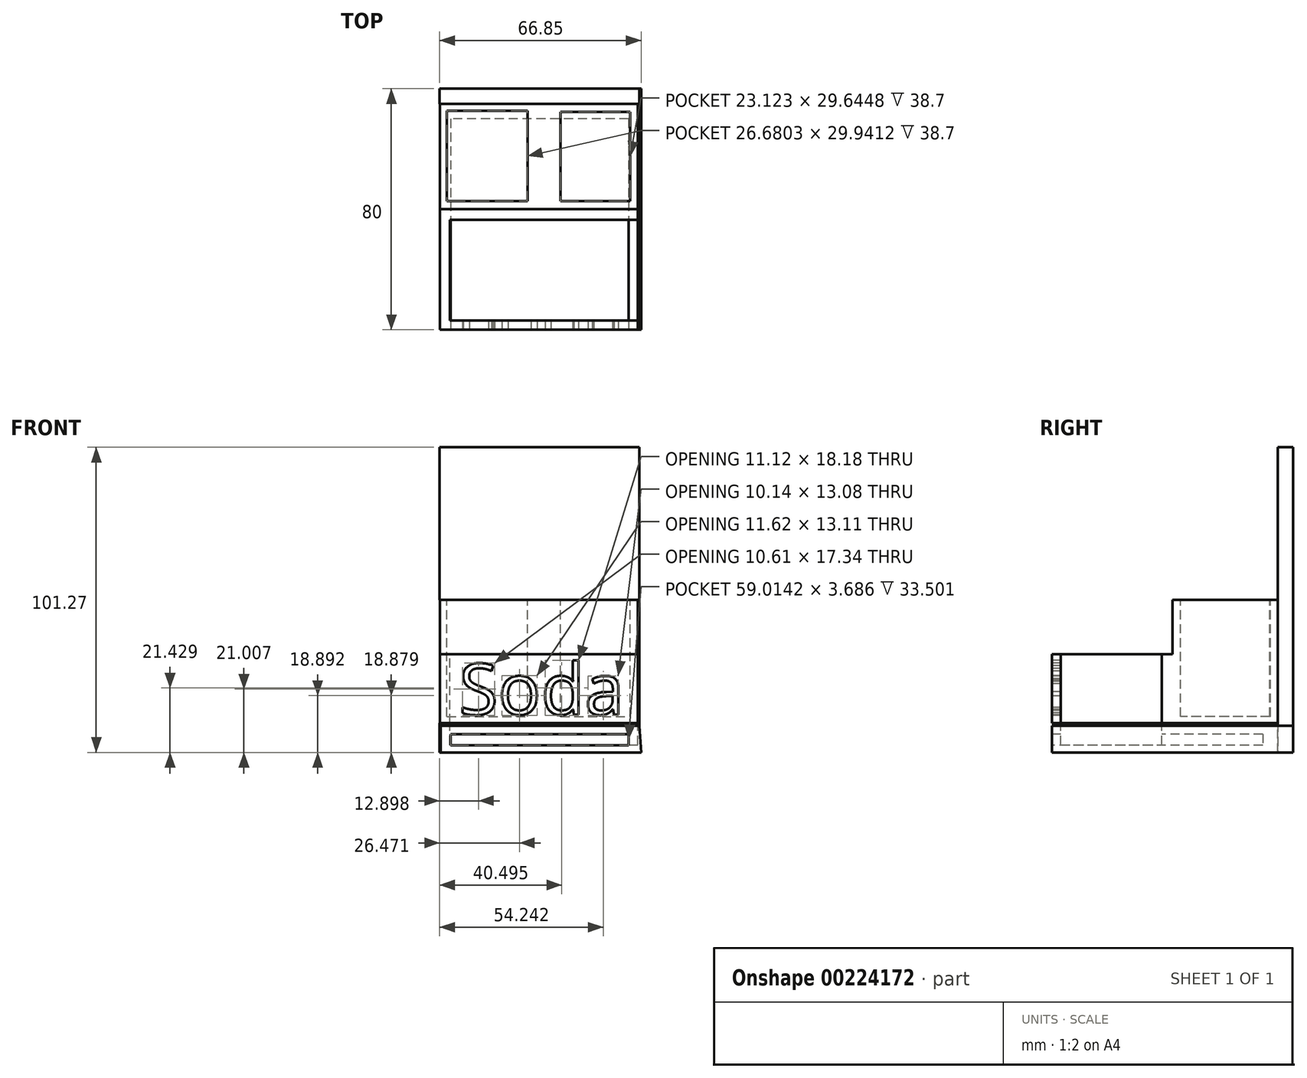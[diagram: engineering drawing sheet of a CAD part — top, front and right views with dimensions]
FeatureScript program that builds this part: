
annotation { "Feature Type Name" : "Feature", "Feature Type Description" : "" }
export const myFeature = defineFeature(function(context is Context, id is Id, definition is map)
    precondition{}
    {
        {
            var Q0;
            Q0=qCreatedBy(makeId("Front.planeOp"),FACE);
            var sketch = newSketch(context, id + "F0", { "sketchPlane" : qUnion([Q0])});
            skLineSegment(sketch, "E0.bottom", {"start": v(-34.43, 50.63) * mm, "end": v(31.85, 50.63) * mm});
            skLineSegment(sketch, "E0.top", {"start": v(-34.43, -50.63) * mm, "end": v(31.85, -50.63) * mm});
            skLineSegment(sketch, "E0.left", {"start": v(-34.43, 50.63) * mm, "end": v(-34.43, -50.63) * mm});
            skLineSegment(sketch, "E0.right", {"start": v(31.85, 50.63) * mm, "end": v(31.85, -50.63) * mm});
            skSolve(sketch);
        }
        {
            var Q0;
            Q0=makeQuery(id+"F0.imprint","IMPRINT",FACE,{"disambiguationData":[TD([[makeQuery(id+"F0.imprint","IMPRINT",EDGE,{"derivedFrom":sQuery(id+"F0.wireOp",EDGE,"E0.bottom")}),-1.0]])]});
            extrude(context, id + "F1", {"entities" : qUnion([Q0]), "depth" : 5 * mm});
        }
        {
            var Q0;
            Q0=qCreatedBy(makeId("Front.planeOp"),FACE);
            var sketch = newSketch(context, id + "F2", { "sketchPlane" : qUnion([Q0])});
            skLineSegment(sketch, "E1", {"start": v(-34.14, -41.74) * mm, "end": v(31.84, -41.74) * mm});
            skLineSegment(sketch, "E2", {"start": v(-34.14, -41.74) * mm, "end": v(-34.14, -50.64) * mm});
            skLineSegment(sketch, "E3", {"start": v(-34.14, -50.64) * mm, "end": v(32.42, -50.64) * mm});
            skLineSegment(sketch, "E4", {"start": v(32.42, -50.64) * mm, "end": v(31.84, -41.74) * mm});
            skSolve(sketch);
        }
        {
            var Q0;
            Q0 = qSketchRegion(id + "F2", true);
            extrude(context, id + "F3", {"entities" : qUnion([Q0]), "operationType" : NewBodyOperationType.ADD, "depth" : 80 * mm});
        }
        {
            var Q0;
            Q0=makeQuery(id+"F3.opExtrude","CAP_FACE",FACE,{"disambiguationData":[OSD([sQuery(id+"F2.wireOp",EDGE,"E1"),sQuery(id+"F2.wireOp",EDGE,"E2"),sQuery(id+"F2.wireOp",EDGE,"E3"),sQuery(id+"F2.wireOp",EDGE,"E4")])],"isStart":false});
            var sketch = newSketch(context, id + "F4", { "sketchPlane" : qUnion([Q0])});
            skLineSegment(sketch, "E5.bottom", {"start": v(28.24, -44.55) * mm, "end": v(-30.78, -44.55) * mm});
            skLineSegment(sketch, "E5.top", {"start": v(28.24, -48.23) * mm, "end": v(-30.78, -48.23) * mm});
            skLineSegment(sketch, "E5.left", {"start": v(28.24, -44.55) * mm, "end": v(28.24, -48.23) * mm});
            skLineSegment(sketch, "E5.right", {"start": v(-30.78, -44.55) * mm, "end": v(-30.78, -48.23) * mm});
            skSolve(sketch);
        }
        {
            var Q0;
            Q0=makeQuery(id+"F4.imprint","IMPRINT",FACE,{"disambiguationData":[TD([[makeQuery(id+"F4.imprint","IMPRINT",EDGE,{"derivedFrom":sQuery(id+"F4.wireOp",EDGE,"E5.bottom")}),1.0]])]});
            extrude(context, id + "F5", {"entities" : qUnion([Q0]), "operationType" : NewBodyOperationType.REMOVE, "oppositeDirection" : true, "depth" : 70 * mm});
        }
        {
            var Q0;
            Q0=qCreatedBy(makeId("Front.planeOp"),FACE);
            var sketch = newSketch(context, id + "F6", { "sketchPlane" : qUnion([Q0])});
            skLineSegment(sketch, "E6.bottom", {"start": v(-34.43, 0) * mm, "end": v(0, 0) * mm});
            skLineSegment(sketch, "E6.top", {"start": v(-34.43, -40.88) * mm, "end": v(0, -40.88) * mm});
            skLineSegment(sketch, "E6.left", {"start": v(-34.43, 0) * mm, "end": v(-34.43, -40.88) * mm});
            skLineSegment(sketch, "E6.right", {"start": v(0, 0) * mm, "end": v(0, -40.88) * mm});
            skLineSegment(sketch, "E7.bottom", {"start": v(0, 0) * mm, "end": v(31.27, 0) * mm});
            skLineSegment(sketch, "E7.top", {"start": v(0, -40.88) * mm, "end": v(31.27, -40.88) * mm});
            skLineSegment(sketch, "E7.right", {"start": v(31.27, 0) * mm, "end": v(31.27, -40.88) * mm});
            skSolve(sketch);
        }
        {
            var Q0;
            Q0 = qSketchRegion(id + "F6", true);
            extrude(context, id + "F7", {"entities" : qUnion([Q0]), "operationType" : NewBodyOperationType.ADD, "depth" : 40 * mm});
        }
        {
            var Q0;
            Q0=qCreatedBy(makeId("Top.planeOp"),FACE);
            var sketch = newSketch(context, id + "F8", { "sketchPlane" : qUnion([Q0])});
            skLineSegment(sketch, "E8.bottom", {"start": v(-32.02, -7.4) * mm, "end": v(-5.34, -7.4) * mm});
            skLineSegment(sketch, "E8.top", {"start": v(-32.02, -37.33) * mm, "end": v(-5.34, -37.33) * mm});
            skLineSegment(sketch, "E8.left", {"start": v(-32.02, -7.4) * mm, "end": v(-32.02, -37.33) * mm});
            skLineSegment(sketch, "E8.right", {"start": v(-5.34, -7.4) * mm, "end": v(-5.34, -37.33) * mm});
            skLineSegment(sketch, "E9.bottom", {"start": v(5.63, -7.69) * mm, "end": v(28.76, -7.69) * mm});
            skLineSegment(sketch, "E9.top", {"start": v(5.63, -37.33) * mm, "end": v(28.76, -37.33) * mm});
            skLineSegment(sketch, "E9.left", {"start": v(5.63, -7.69) * mm, "end": v(5.63, -37.33) * mm});
            skLineSegment(sketch, "E9.right", {"start": v(28.76, -7.69) * mm, "end": v(28.76, -37.33) * mm});
            skSolve(sketch);
        }
        {
            var Q0;
            Q0 = qSketchRegion(id + "F8", true);
            extrude(context, id + "F9", {"entities" : qUnion([Q0]), "operationType" : NewBodyOperationType.REMOVE, "oppositeDirection" : true, "depth" : 38.7 * mm});
        }
        {
            var Q0;
            Q0=makeQuery(id+"F7.opExtrude","CAP_FACE",FACE,{"disambiguationData":[OSD([sQuery(id+"F6.wireOp",EDGE,"E6.bottom"),sQuery(id+"F6.wireOp",EDGE,"E6.top"),sQuery(id+"F6.wireOp",EDGE,"E6.left"),sQuery(id+"F6.wireOp",EDGE,"E7.bottom"),sQuery(id+"F6.wireOp",EDGE,"E7.top"),sQuery(id+"F6.wireOp",EDGE,"E7.right")])],"isStart":false});
            var sketch = newSketch(context, id + "F10", { "sketchPlane" : qUnion([Q0])});
            skLineSegment(sketch, "E10.bottom", {"start": v(-34.43, -18.1) * mm, "end": v(31.27, -18.1) * mm});
            skLineSegment(sketch, "E10.top", {"start": v(-34.43, -40.88) * mm, "end": v(31.27, -40.88) * mm});
            skLineSegment(sketch, "E10.left", {"start": v(-34.43, -18.1) * mm, "end": v(-34.43, -40.88) * mm});
            skLineSegment(sketch, "E10.right", {"start": v(31.27, -18.1) * mm, "end": v(31.27, -40.88) * mm});
            skSolve(sketch);
        }
        {
            var Q0;
            Q0 = qSketchRegion(id + "F10", true);
            extrude(context, id + "F11", {"entities" : qUnion([Q0]), "operationType" : NewBodyOperationType.ADD, "depth" : 40 * mm});
        }
        {
            var Q0;
            Q0=makeQuery(id+"F11.opExtrude","SWEPT_FACE",FACE,{"disambiguationData":[OSD([sQuery(id+"F10.wireOp",EDGE,"E10.bottom")])]});
            var sketch = newSketch(context, id + "F12", { "sketchPlane" : qUnion([Q0])});
            skLineSegment(sketch, "E11.bottom", {"start": v(-31, -43.5) * mm, "end": v(31.27, -43.5) * mm});
            skLineSegment(sketch, "E11.top", {"start": v(-31, -76.98) * mm, "end": v(31.27, -76.98) * mm});
            skLineSegment(sketch, "E11.left", {"start": v(-31, -43.5) * mm, "end": v(-31, -76.98) * mm});
            skLineSegment(sketch, "E11.right", {"start": v(31.27, -43.5) * mm, "end": v(31.27, -76.98) * mm});
            skSolve(sketch);
        }
        {
            var Q0;
            Q0 = qSketchRegion(id + "F12", true);
            extrude(context, id + "F13", {"entities" : qUnion([Q0]), "operationType" : NewBodyOperationType.REMOVE, "oppositeDirection" : true, "depth" : 30 * mm});
        }
        {
            var Q0;
            Q0=makeQuery(id+"F11.opExtrude","CAP_FACE",FACE,{"disambiguationData":[OSD([sQuery(id+"F10.wireOp",EDGE,"E10.bottom"),sQuery(id+"F10.wireOp",EDGE,"E10.top"),sQuery(id+"F10.wireOp",EDGE,"E10.left"),sQuery(id+"F10.wireOp",EDGE,"E10.right")])],"isStart":false});
            var sketch = newSketch(context, id + "F14", { "sketchPlane" : qUnion([Q0])});
            skText(sketch, "E12", { "text": "Soda", "fontName": "OpenSans-Regular.ttf"});
            const initialGuessF14  = {"E12": [-0.02806, -0.03807, 1, 0, 0.01701]};
            skSetInitialGuess(sketch, initialGuessF14);
            skSolve(sketch);
        }
        {
            var Q0;
            Q0 = qSketchRegion(id + "F14", true);
            extrude(context, id + "F15", {"entities" : qUnion([Q0]), "operationType" : NewBodyOperationType.REMOVE, "oppositeDirection" : true, "depth" : 5 * mm});
        }
    });
